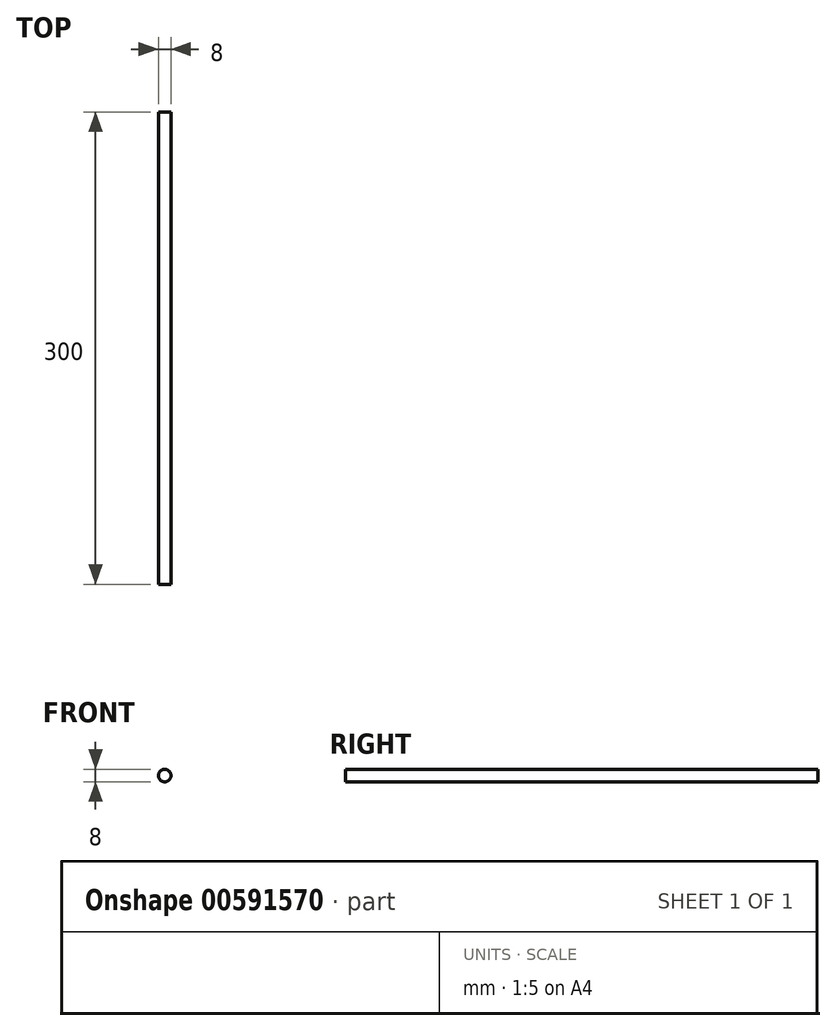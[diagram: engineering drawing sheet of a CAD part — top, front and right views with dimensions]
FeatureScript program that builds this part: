
annotation { "Feature Type Name" : "Feature", "Feature Type Description" : "" }
export const myFeature = defineFeature(function(context is Context, id is Id, definition is map)
    precondition{}
    {
        {
            var Q0;
            Q0=qCreatedBy(makeId("Front.planeOp"),FACE);
            var sketch = newSketch(context, id + "F0", { "sketchPlane" : qUnion([Q0])});
            skCircle(sketch, "E0", {"center": v(0, 0) * mm, "radius": 4 * mm});
            skSolve(sketch);
        }
        {
            var Q0;
            Q0 = qSketchRegion(id + "F0", true);
            extrude(context, id + "F1", {"entities" : qUnion([Q0]), "depth" : 300 * mm, "offsetDistance" : 25 * mm});
        }
    });
